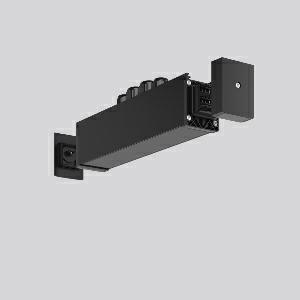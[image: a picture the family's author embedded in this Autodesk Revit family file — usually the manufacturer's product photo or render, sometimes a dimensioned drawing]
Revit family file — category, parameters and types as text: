
# Revit family: linedo_universaleinspeisung_14pol_b_s_982698_003_6_6357
name_source: partatom
category: Lighting Fixtures
units: mm (PartAtom-declared; Revit-internal decimal feet)

## family parameters
Cut with Voids When Loaded = No
Host = Face
Light Source = No
Part Type = Normal
Room Calculation Point = No
Round Connector Dimension = Use Diameter
Shared = No

## types (1)
- LINEDO_Universaleinspeisung_14pol_B_S
    Apparent Load = 0 VA
    Default Elevation = 1800 mm
    Description = Series: LINEDO
Universal power feed that can be used as initial or central feed for flexible installation on site. 14-pole, connection socket / plug. Housing: extruded aluminium profile, powder-coated. Cover made of plastic, surface like housing. LINEDO plug system, plastic, black. Incl. end caps. 4 cable glands (2 x M20 and 2 x M25). Cable glands on top. Easy connection for rigid or flexible wires.
Colour: black
Length: 330 mm
Width: 58 mm
Height: 76 mm
Weight: 913 g
    Height = 76 mm
    Lamp = 0 x
    Length = 330 mm
    Luminous efficacy = 0 lm/W
    Manufacturer = RZB
    ModVariant = No
    Model = 982698.003.6
    Mounting Place = Ceiling
    Mounting Type = Surface mounted
    Number of Poles = 1
    OnlyDefault = Yes
    Power Factor = 1
    Product Name = LINEDO_Universaleinspeisung_14pol_B_S
    Product group = Surface mounted continuous line luminaire system
    ProductGroupID = 310
    Protection Class = Protection class I
    Protection Degree = Degree of protection
    RLX_Detail_Level = 1
    RLX_Emergency_Light_Flux = 0 lm
    RLX_Emergency_Type = 0
    RLX_Emergency_Type_DB = No
    RlxData = <blob elided: 18789 chars, md5=c2d5d196>
    Standby Power = 0 W
    System Light Flux = 0 lm
    System Power = 0 W
    Type Comments = Product without accessories
    Type Image = 982698.003.6.jpg
    URL = http://relux.com
    VarID = ---
    Voltage = 0 V
    Weight = 0.00 kg
    Width = 58 mm

## geometry (parser evidence)
native form markers: Blend x4, Sweep x11
no freeform markers — native parametric forms only
